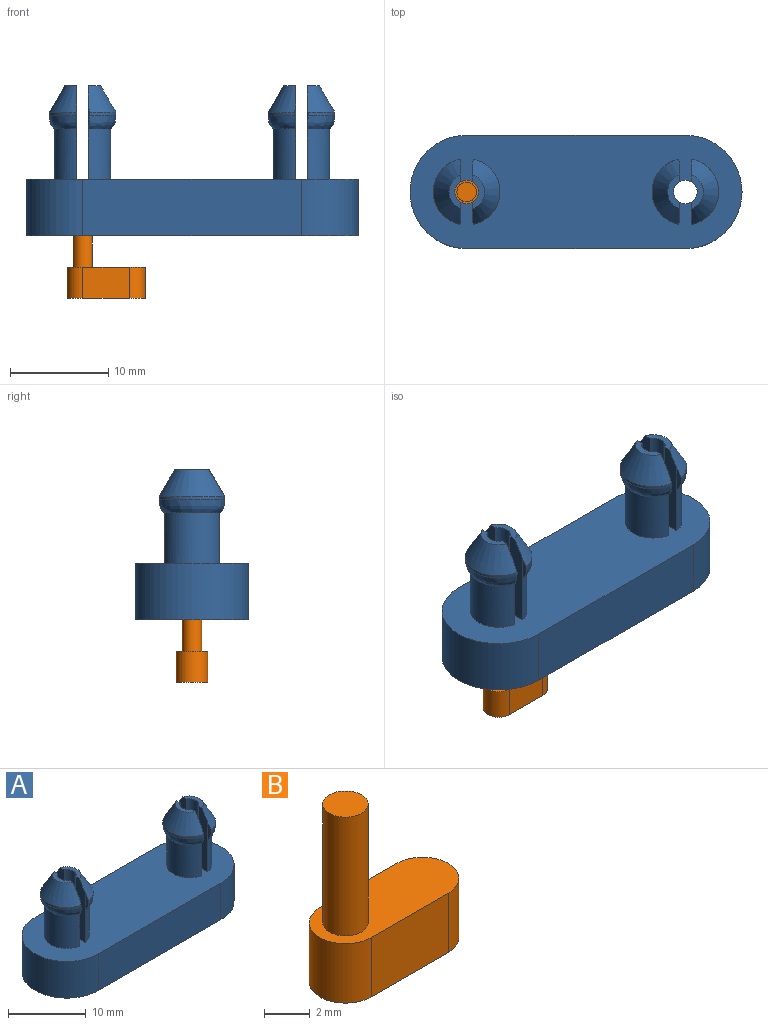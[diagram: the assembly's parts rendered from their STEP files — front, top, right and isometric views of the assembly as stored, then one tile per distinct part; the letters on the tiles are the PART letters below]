
ASSEMBLY  parts=2 mates=1
PART A: 68 faces, bbox 33.9x11.6x15.4 mm
  f0: plane 22.23x5.75mm, normal (0,1,0), area 127.9mm2, adj f1,f25,f26,f27
  f1: cylinder r=5.75mm len=11.51mm, axis (0,0,1), area 104mm2, adj f0,f2,f26,f27
  f2: plane 22.23x5.75mm, normal (0,-1,0), area 127.9mm2, adj f1,f25,f26,f27
  f3: plane 1.78x0.04mm, normal (-1,0,0), area 0.1mm2, adj f4,f8,f26,f48
  f4: plane 0.5x0.1mm, normal (-0.98,0.2,0), area 0mm2, adj f3,f5,f26,f48
  f5: cylinder r=3.39mm len=6.63mm, axis (0,0,1), area 0.4mm2, adj f4,f6,f26,f48
  f6: plane 0.5x0.1mm, normal (-0.98,-0.2,0), area 0mm2, adj f5,f7,f26,f48
  f7: plane 1.78x0.04mm, normal (-1,0,0), area 0.1mm2, adj f6,f8,f26,f48
  f8: cylinder r=1.19mm len=15.28mm, axis (0,0,1), area 91.1mm2, adj f3,f7,f9,f23,f26,f27,f45,f46
  f9: plane 1.78x0.04mm, normal (1,0,0), area 0.1mm2, adj f8,f10,f26,f55
  f10: plane 0.5x0.1mm, normal (0.98,-0.2,0), area 0mm2, adj f9,f11,f26,f55
  f11: cylinder r=3.39mm len=6.63mm, axis (0,0,1), area 0.4mm2, adj f10,f12,f26,f55
  f12: plane 0.5x0.1mm, normal (0.98,0.2,0), area 0mm2, adj f11,f23,f26,f55
  f13: plane 1.78x0.04mm, normal (-1,0,0), area 0.1mm2, adj f14,f18,f26,f34
  f14: plane 0.5x0.1mm, normal (-0.98,0.2,0), area 0mm2, adj f13,f15,f26,f34
  f15: cylinder r=3.39mm len=6.63mm, axis (0,0,1), area 0.4mm2, adj f14,f16,f26,f34
  f16: plane 0.5x0.1mm, normal (-0.98,-0.2,0), area 0mm2, adj f15,f17,f26,f34
  f17: plane 1.78x0.04mm, normal (-1,0,0), area 0.1mm2, adj f16,f18,f26,f34
  f18: cylinder r=1.19mm len=15.28mm, axis (0,0,1), area 91.1mm2, adj f13,f17,f19,f24,f26,f27,f28,f29
  f19: plane 1.78x0.04mm, normal (1,0,0), area 0.1mm2, adj f18,f20,f26,f41
  f20: plane 0.5x0.1mm, normal (0.98,-0.2,0), area 0mm2, adj f19,f21,f26,f41
  f21: cylinder r=3.39mm len=6.63mm, axis (0,0,1), area 0.4mm2, adj f20,f22,f26,f41
  f22: plane 0.5x0.1mm, normal (0.98,0.2,0), area 0mm2, adj f21,f24,f26,f41
  f23: plane 1.78x0.04mm, normal (1,0,0), area 0.1mm2, adj f8,f12,f26,f55
  f24: plane 1.78x0.04mm, normal (1,0,0), area 0.1mm2, adj f18,f22,f26,f41
  f25: cylinder r=5.75mm len=11.51mm, axis (0,0,1), area 104mm2, adj f0,f2,f26,f27
  f26: plane 33.73x11.51mm, normal (0,0,-1), area 298.3mm2, adj f0,f1,f2,f3,f4,f5,f6,f7
  f27: plane 33.73x11.51mm, normal (0,0,1), area 315.7mm2, adj f0,f1,f2,f8,f18,f25,f28,f29
  f28: plane 9.59x1.85mm, normal (1,0,0), area 15.9mm2, adj f18,f27,f32,f33,f59,f60
  f29: plane 9.59x1.85mm, normal (1,0,0), area 15.9mm2, adj f18,f27,f30,f33,f59,f60
  f30: plane 2.66x0.62mm, normal (0.98,0.2,0), area 0.9mm2, adj f29,f31,f60,f66
  f31: cylinder r=3.39mm len=6.63mm, axis (0,0,-1), area 2.8mm2, adj f30,f32,f60,f66
  f32: plane 2.65x0.62mm, normal (0.98,-0.2,0), area 0.9mm2, adj f28,f31,f60,f66
  f33: plane 3.41x1.22mm, normal (0,0,1), area 2.1mm2, adj f18,f28,f29,f60
  f34: plane 6.63x2.81mm, normal (0,0,-1), area 13.2mm2, adj f13,f14,f15,f16,f17,f18
  f35: plane 9.59x1.84mm, normal (-1,0,0), area 16mm2, adj f18,f27,f36,f40,f58,f62
  f36: plane 2.71x0.62mm, normal (-0.98,-0.2,0), area 0.9mm2, adj f35,f37,f62,f67
  f37: cylinder r=3.39mm len=6.63mm, axis (0,0,-1), area 3.3mm2, adj f36,f38,f62,f67
  f38: plane 2.71x0.62mm, normal (-0.98,0.2,0), area 0.9mm2, adj f37,f39,f62,f67
  f39: plane 9.59x1.84mm, normal (-1,0,0), area 16mm2, adj f18,f27,f38,f40,f58,f62
  f40: plane 3.47x1.25mm, normal (0,0,1), area 2.3mm2, adj f18,f35,f39,f62
  f41: plane 6.63x2.81mm, normal (0,0,-1), area 13.2mm2, adj f18,f19,f20,f21,f22,f24
  f42: plane 2.66x0.62mm, normal (0.98,0.2,0), area 0.9mm2, adj f43,f46,f61,f65
  f43: cylinder r=3.39mm len=6.63mm, axis (0,0,-1), area 2.8mm2, adj f42,f44,f61,f65
  f44: plane 2.65x0.62mm, normal (0.98,-0.2,0), area 0.9mm2, adj f43,f45,f61,f65
  f45: plane 9.59x1.85mm, normal (1,0,0), area 15.9mm2, adj f8,f27,f44,f47,f57,f61
  f46: plane 9.59x1.85mm, normal (1,0,0), area 15.9mm2, adj f8,f27,f42,f47,f57,f61
  f47: plane 3.41x1.22mm, normal (0,0,1), area 2.1mm2, adj f8,f45,f46,f61
  f48: plane 6.63x2.81mm, normal (0,0,-1), area 13.2mm2, adj f3,f4,f5,f6,f7,f8
  f49: plane 9.59x1.84mm, normal (-1,0,0), area 16mm2, adj f8,f27,f50,f54,f56,f63
  f50: plane 2.71x0.62mm, normal (-0.98,-0.2,0), area 0.9mm2, adj f49,f51,f63,f64
  f51: cylinder r=3.39mm len=6.63mm, axis (0,0,-1), area 3.3mm2, adj f50,f52,f63,f64
  f52: plane 2.71x0.62mm, normal (-0.98,0.2,0), area 0.9mm2, adj f51,f53,f63,f64
  f53: plane 9.59x1.84mm, normal (-1,0,0), area 16mm2, adj f8,f27,f52,f54,f56,f63
  f54: plane 3.47x1.25mm, normal (0,0,1), area 2.3mm2, adj f8,f49,f53,f63
  f55: plane 6.63x2.81mm, normal (0,0,-1), area 13.2mm2, adj f8,f9,f10,f11,f12,f23
  f56: cylinder r=2.88mm len=5.64mm, axis (0,0,-1), area 40.3mm2, adj f27,f49,f53,f64
  f57: cylinder r=2.88mm len=5.64mm, axis (0,0,-1), area 40.3mm2, adj f27,f45,f46,f65
  f58: cylinder r=2.88mm len=5.64mm, axis (0,0,-1), area 40.3mm2, adj f27,f35,f39,f67
  f59: cylinder r=2.88mm len=5.64mm, axis (0,0,-1), area 40.3mm2, adj f27,f28,f29,f66
  f60: cone r=3.39mm half-angle=30deg, axis (0,0,-1), area 21.9mm2, adj f28,f29,f30,f31,f32,f33
  f61: cone r=3.39mm half-angle=30deg, axis (0,0,-1), area 21.9mm2, adj f42,f43,f44,f45,f46,f47
  f62: cone r=1.83mm half-angle=30deg, axis (0,0,-1), area 21.7mm2, adj f35,f36,f37,f38,f39,f40
  f63: cone r=1.83mm half-angle=30deg, axis (0,0,-1), area 21.7mm2, adj f49,f50,f51,f52,f53,f54
  f64: bspline ~6.76x3.61mm, area 13.3mm2, adj f50,f51,f52,f56
  f65: bspline ~6.76x3.61mm, area 13.3mm2, adj f42,f43,f44,f57
  f66: bspline ~6.76x3.61mm, area 13.3mm2, adj f30,f31,f32,f59
  f67: bspline ~6.76x3.61mm, area 13.3mm2, adj f36,f37,f38,f58
PART B: 8 faces, bbox 7.9x3.2x9.5 mm
  f0: cylinder r=0.99mm len=6.35mm, axis (0,0,-1), area 39.6mm2, adj f1,f6
  f1: plane 1.98x1.98mm, normal (0,0,1), area 3.1mm2, adj f0
  f2: plane 4.76x3.18mm, normal (0,-1,0), area 15.1mm2, adj f3,f5,f6,f7
  f3: cylinder r=1.59mm len=3.18mm, axis (0,0,-1), area 15.8mm2, adj f2,f4,f6,f7
  f4: plane 4.76x3.18mm, normal (0,1,0), area 15.1mm2, adj f3,f5,f6,f7
  f5: cylinder r=1.59mm len=3.18mm, axis (0,0,-1), area 15.8mm2, adj f2,f4,f6,f7
  f6: plane 7.94x3.18mm, normal (0,0,1), area 19.9mm2, adj f0,f2,f3,f4,f5
  f7: plane 7.94x3.18mm, normal (0,0,-1), area 23mm2, adj f2,f3,f4,f5
PLACE A t=(-16.57,-6.97,-2.92)mm
PLACE B t=(-27.68,-6.97,-15.03)mm
MATE fastened B.f0 <-> A.f1  axis (0,0,-1) through (-27.68,-6.97,-8.68)mm
